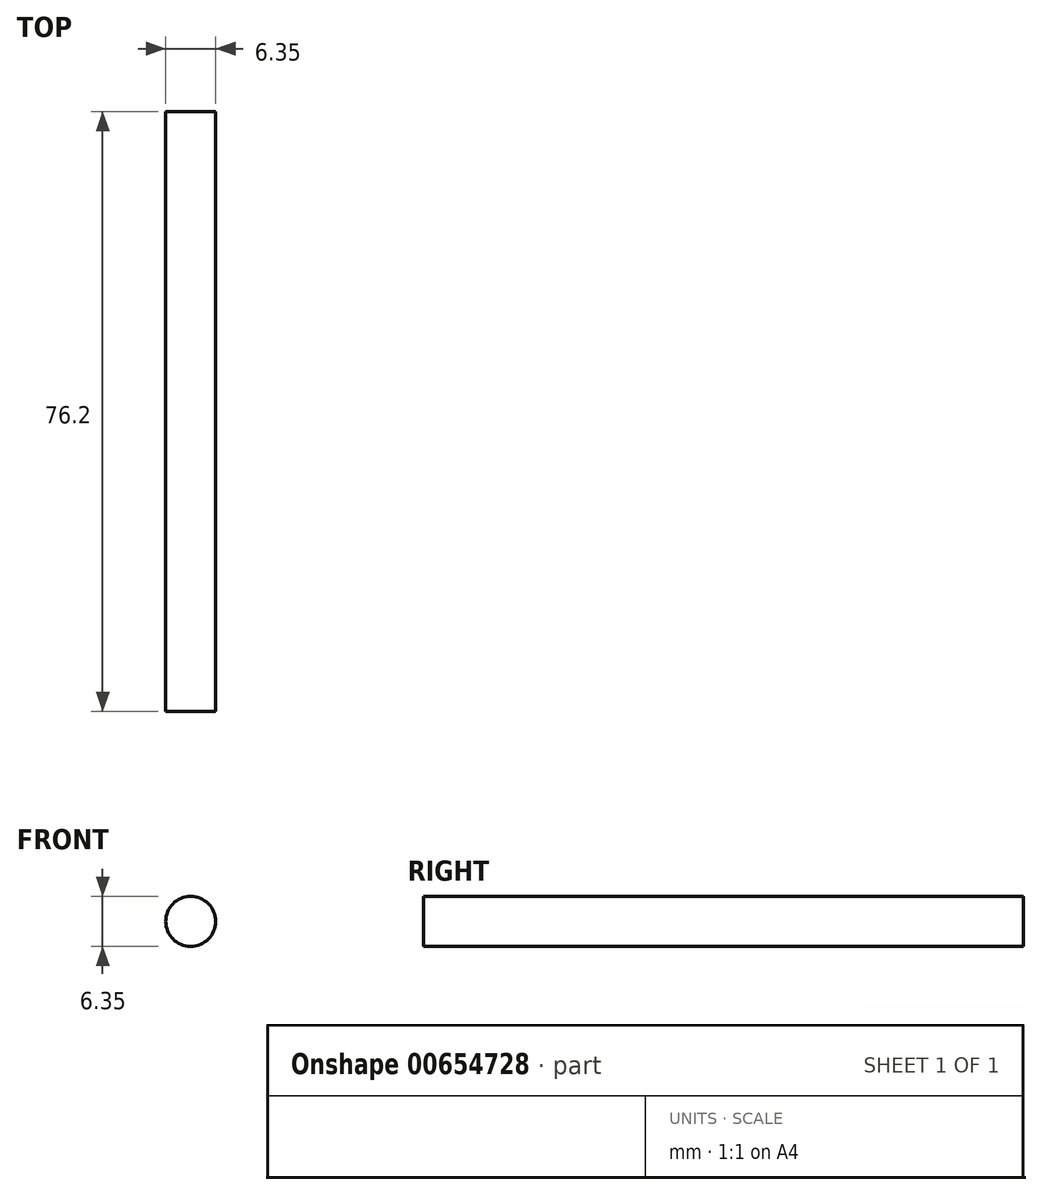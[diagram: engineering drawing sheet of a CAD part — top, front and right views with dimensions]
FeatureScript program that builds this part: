
annotation { "Feature Type Name" : "Feature", "Feature Type Description" : "" }
export const myFeature = defineFeature(function(context is Context, id is Id, definition is map)
    precondition{}
    {
        {
            var Q0;
            Q0=qCreatedBy(makeId("Front.planeOp"),FACE);
            var sketch = newSketch(context, id + "F0", { "sketchPlane" : qUnion([Q0])});
            skCircle(sketch, "E0", {"center": v(8.15, 16.4) * mm, "radius": 3.18 * mm});
            skSolve(sketch);
        }
        {
            var Q0;
            Q0 = qSketchRegion(id + "F0", true);
            extrude(context, id + "F1", {"entities" : qUnion([Q0]), "depth" : 76.2 * mm, "offsetDistance" : 25.4 * mm});
        }
    });
